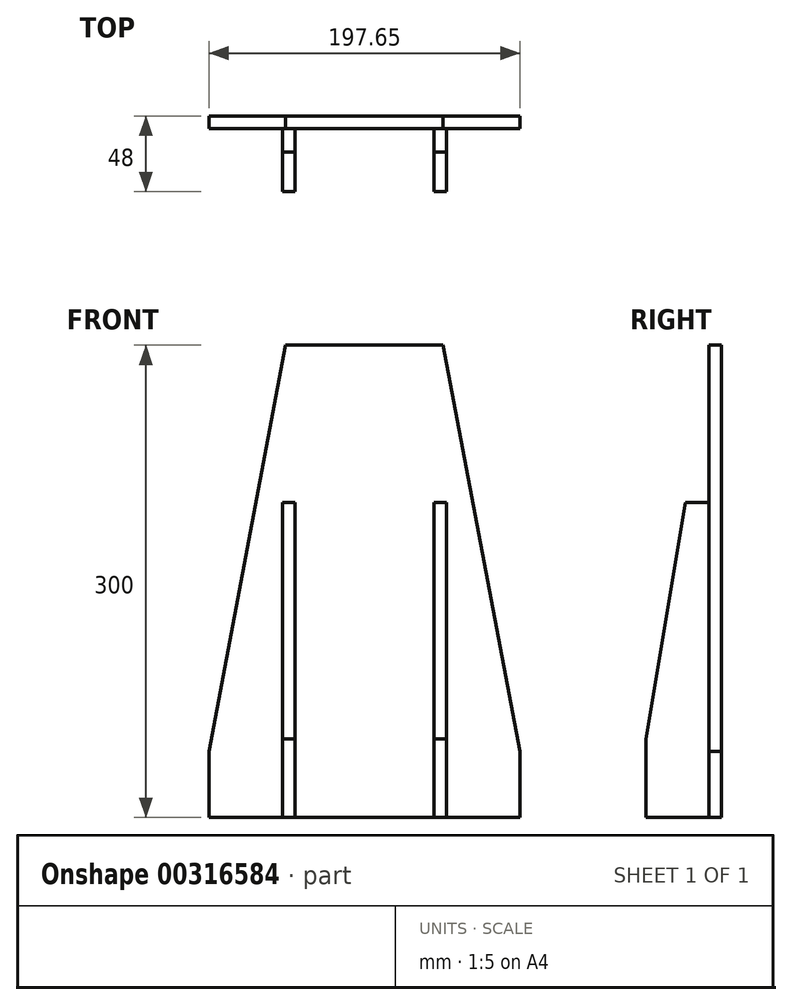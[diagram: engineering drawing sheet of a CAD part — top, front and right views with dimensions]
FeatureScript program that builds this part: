
annotation { "Feature Type Name" : "Feature", "Feature Type Description" : "" }
export const myFeature = defineFeature(function(context is Context, id is Id, definition is map)
    precondition{}
    {
        {
            var Q0;
            Q0=qCreatedBy(makeId("Front.planeOp"),FACE);
            var sketch = newSketch(context, id + "F0", { "sketchPlane" : qUnion([Q0])});
            skLineSegment(sketch, "E0", {"start": v(0, 0) * mm, "end": v(197.65, 0) * mm});
            skLineSegment(sketch, "E1", {"start": v(197.65, 0) * mm, "end": v(197.65, 42) * mm});
            skLineSegment(sketch, "E2", {"start": v(98.83, 0) * mm, "end": v(98.83, 300) * mm});
            skLineSegment(sketch, "E3", {"start": v(98.83, 300) * mm, "end": v(148.82, 300) * mm});
            skLineSegment(sketch, "E4", {"start": v(148.82, 300) * mm, "end": v(197.65, 42) * mm});
            skLineSegment(sketch, "E5", {"start": v(98.83, 300) * mm, "end": v(48.83, 300) * mm});
            skLineSegment(sketch, "E6", {"start": v(0, 0) * mm, "end": v(0, 42) * mm});
            skLineSegment(sketch, "E7", {"start": v(0, 42) * mm, "end": v(48.83, 300) * mm});
            skSolve(sketch);
        }
        {
            var Q0;
            {var subQ1=sQuery(id+"F0.wireOp",EDGE,"E2");Q0=makeQuery(id+"F0.imprint","IMPRINT",FACE,{"disambiguationData":[TD([[makeQuery(id+"F0.imprint","IMPRINT",EDGE,{"derivedFrom":subQ1}),1.0]])]});}
            var Q1;
            {var subQ1=sQuery(id+"F0.wireOp",EDGE,"E1");Q1=makeQuery(id+"F0.imprint","IMPRINT",FACE,{"disambiguationData":[TD([[makeQuery(id+"F0.imprint","IMPRINT",EDGE,{"derivedFrom":subQ1}),1.0]])]});}
            extrude(context, id + "F1", {"entities" : qUnion([Q0, Q1]), "depth" : 8 * mm});
        }
        {
            var Q0;
            Q0=makeQuery(id+"F1.opExtrude","CAP_FACE",FACE,{"disambiguationData":[OSD([sQuery(id+"F0.wireOp",EDGE,"E0"),sQuery(id+"F0.wireOp",EDGE,"E1"),sQuery(id+"F0.wireOp",EDGE,"E3"),sQuery(id+"F0.wireOp",EDGE,"E4"),sQuery(id+"F0.wireOp",EDGE,"E5"),sQuery(id+"F0.wireOp",EDGE,"E6"),sQuery(id+"F0.wireOp",EDGE,"E7")])],"isStart":false});
            var sketch = newSketch(context, id + "F2", { "sketchPlane" : qUnion([Q0])});
            skLineSegment(sketch, "E8", {"start": v(46.67, 0) * mm, "end": v(46.67, 200) * mm});
            skLineSegment(sketch, "E9", {"start": v(46.67, 200) * mm, "end": v(54.67, 200) * mm});
            skLineSegment(sketch, "E10", {"start": v(54.67, 200) * mm, "end": v(54.67, 0) * mm});
            skLineSegment(sketch, "E11", {"start": v(54.67, 0) * mm, "end": v(46.67, 0) * mm});
            skLineSegment(sketch, "E12", {"start": v(197.65, 0) * mm, "end": v(150.98, 0) * mm});
            skLineSegment(sketch, "E13", {"start": v(150.98, 0) * mm, "end": v(150.98, 200) * mm});
            skLineSegment(sketch, "E14", {"start": v(150.98, 200) * mm, "end": v(142.98, 200) * mm});
            skLineSegment(sketch, "E15", {"start": v(142.98, 200) * mm, "end": v(142.98, 0) * mm});
            skLineSegment(sketch, "E16", {"start": v(142.98, 0) * mm, "end": v(150.98, 0) * mm});
            skSolve(sketch);
        }
        {
            var Q0;
            Q0=makeQuery(id+"F2.imprint","IMPRINT",FACE,{"disambiguationData":[TD([[makeQuery(id+"F2.imprint","IMPRINT",EDGE,{"derivedFrom":sQuery(id+"F2.wireOp",EDGE,"E8")}),-1.0]])]});
            var Q1;
            Q1=makeQuery(id+"F2.imprint","IMPRINT",FACE,{"disambiguationData":[TD([[makeQuery(id+"F2.imprint","IMPRINT",EDGE,{"derivedFrom":sQuery(id+"F2.wireOp",EDGE,"E13")}),1.0]])]});
            extrude(context, id + "F3", {"entities" : qUnion([Q0, Q1]), "operationType" : NewBodyOperationType.ADD, "depth" : 40 * mm});
        }
        {
            var Q0;
            Q0=makeQuery(id+"F3.opExtrude","SWEPT_FACE",FACE,{"disambiguationData":[OSD([sQuery(id+"F2.wireOp",EDGE,"E8")])]});
            var sketch = newSketch(context, id + "F4", { "sketchPlane" : qUnion([Q0])});
            skLineSegment(sketch, "E17", {"start": v(48, 0) * mm, "end": v(48, 50) * mm});
            skLineSegment(sketch, "E18", {"start": v(8, 200) * mm, "end": v(23, 200) * mm});
            skLineSegment(sketch, "E19", {"start": v(23, 200) * mm, "end": v(48, 50) * mm});
            skLineSegment(sketch, "E20", {"start": v(48, 200) * mm, "end": v(23, 200) * mm});
            skLineSegment(sketch, "E21", {"start": v(48, 200) * mm, "end": v(48, 50) * mm});
            skSolve(sketch);
        }
        {
            var Q0;
            Q0=makeQuery(id+"F4.imprint","IMPRINT",FACE,{"disambiguationData":[TD([[makeQuery(id+"F4.imprint","IMPRINT",EDGE,{"derivedFrom":sQuery(id+"F4.wireOp",EDGE,"E19")}),1.0]])]});
            extrude(context, id + "F5", {"entities" : qUnion([Q0]), "operationType" : NewBodyOperationType.REMOVE, "oppositeDirection" : true, "depth" : 150 * mm});
        }
    });
